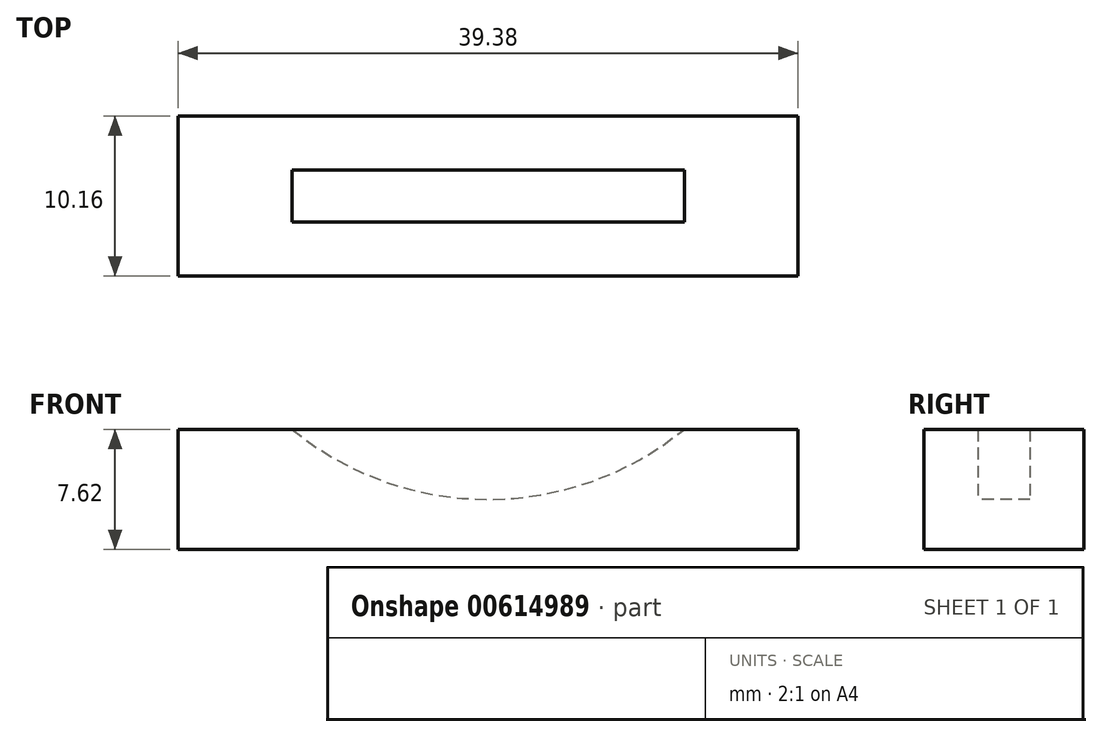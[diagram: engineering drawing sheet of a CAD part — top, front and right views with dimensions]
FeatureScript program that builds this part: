
annotation { "Feature Type Name" : "Feature", "Feature Type Description" : "" }
export const myFeature = defineFeature(function(context is Context, id is Id, definition is map)
    precondition{}
    {
        {
            var Q0;
            Q0=qCreatedBy(makeId("Top.planeOp"),FACE);
            var sketch = newSketch(context, id + "F0", { "sketchPlane" : qUnion([Q0])});
            skLineSegment(sketch, "E0.bottom", {"start": v(19.69, -5.08) * mm, "end": v(-19.69, -5.08) * mm});
            skLineSegment(sketch, "E0.top", {"start": v(19.69, 5.08) * mm, "end": v(-19.69, 5.08) * mm});
            skLineSegment(sketch, "E0.left", {"start": v(19.69, -5.08) * mm, "end": v(19.69, 5.08) * mm});
            skLineSegment(sketch, "E0.right", {"start": v(-19.69, -5.08) * mm, "end": v(-19.69, 5.08) * mm});
            skPoint(sketch, "E0.middle", {"position": v(0, 0) * mm});
            skSolve(sketch);
        }
        {
            var Q0;
            Q0=makeQuery(id+"F0.imprint","IMPRINT",FACE,{"disambiguationData":[TD([[makeQuery(id+"F0.imprint","IMPRINT",EDGE,{"derivedFrom":sQuery(id+"F0.wireOp",EDGE,"E0.bottom")}),-1.0]])]});
            extrude(context, id + "F1", {"entities" : qUnion([Q0]), "depth" : 7.62 * mm, "offsetDistance" : 25.4 * mm});
        }
        {
            var Q0;
            Q0=makeQuery(id+"F1.opExtrude","SWEPT_FACE",FACE,{"disambiguationData":[OSD([sQuery(id+"F0.wireOp",EDGE,"E0.bottom")])]});
            var sketch = newSketch(context, id + "F2", { "sketchPlane" : qUnion([Q0])});
            skLineSegment(sketch, "E1", {"start": v(0, 7.62) * mm, "end": v(0, 0) * mm, "construction": true});
            skCircle(sketch, "E2", {"center": v(0, 22.86) * mm, "radius": 19.69 * mm});
            skPoint(sketch, "E2.first.point", {"position": v(-12.46, 7.62) * mm});
            skPoint(sketch, "E2.second.point", {"position": v(0, 3.18) * mm});
            skPoint(sketch, "E2.third.point", {"position": v(12.46, 7.62) * mm});
            skLineSegment(sketch, "E3", {"start": v(0, 22.86) * mm, "end": v(0, 7.62) * mm, "construction": true});
            skSolve(sketch);
        }
        {
            var Q0;
            Q0 = qSketchRegion(id + "F2", true);
            extrude(context, id + "F3", {"entities" : qUnion([Q0]), "operationType" : NewBodyOperationType.REMOVE, "oppositeDirection" : true, "depth" : 12.7 * mm, "offsetDistance" : 25.4 * mm});
        }
        {
            var Q0;
            {var subQ0=sQuery(id+"F2.wireOp",EDGE,"E2");var subQ1=makeQuery(id+"F1.opExtrude","CAP_EDGE",EDGE,{"disambiguationData":[OSD([sQuery(id+"F0.wireOp",EDGE,"E0.bottom")])],"isStart":false});var subQ2=makeQuery(id+"F2.imprint","INTERSECT",VERTEX,{"disambiguationData":[OD(0.0)],"derivedFrom":[subQ1,subQ0]});Q0=makeQuery(id+"F2.imprint","IMPRINT",FACE,{"disambiguationData":[TD([[makeQuery(id+"F2.imprint","IMPRINT",EDGE,{"disambiguationData":[TD([[subQ2,1.0]])],"derivedFrom":subQ0}),1.0]])]});}
            extrude(context, id + "F4", {"entities" : qUnion([Q0]), "operationType" : NewBodyOperationType.ADD, "oppositeDirection" : true, "depth" : 3.43 * mm, "offsetDistance" : 25.4 * mm});
        }
        {
            var Q0;
            Q0=makeQuery(id+"F1.opExtrude","SWEPT_FACE",FACE,{"disambiguationData":[OSD([sQuery(id+"F0.wireOp",EDGE,"E0.top")])]});
            var sketch = newSketch(context, id + "F5", { "sketchPlane" : qUnion([Q0])});
            skLineSegment(sketch, "E4.bottom", {"start": v(-19.69, 7.62) * mm, "end": v(19.69, 7.62) * mm});
            skLineSegment(sketch, "E4.top", {"start": v(-19.69, 0) * mm, "end": v(19.69, 0) * mm});
            skLineSegment(sketch, "E4.left", {"start": v(-19.69, 7.62) * mm, "end": v(-19.69, 0) * mm});
            skLineSegment(sketch, "E4.right", {"start": v(19.69, 7.62) * mm, "end": v(19.69, 0) * mm});
            skSolve(sketch);
        }
        {
            var Q0;
            Q0 = qSketchRegion(id + "F5", true);
            var Q1;
            Q1=makeQuery(id+"F5.imprint","IMPRINT",FACE,{"disambiguationData":[TD([[makeQuery(id+"F5.imprint","IMPRINT",EDGE,{"derivedFrom":sQuery(id+"F5.wireOp",EDGE,"E4.top")}),1.0]])]});
            extrude(context, id + "F6", {"entities" : qUnion([Q0, Q1]), "operationType" : NewBodyOperationType.ADD, "oppositeDirection" : true, "depth" : 3.43 * mm, "offsetDistance" : 25.4 * mm});
        }
    });
